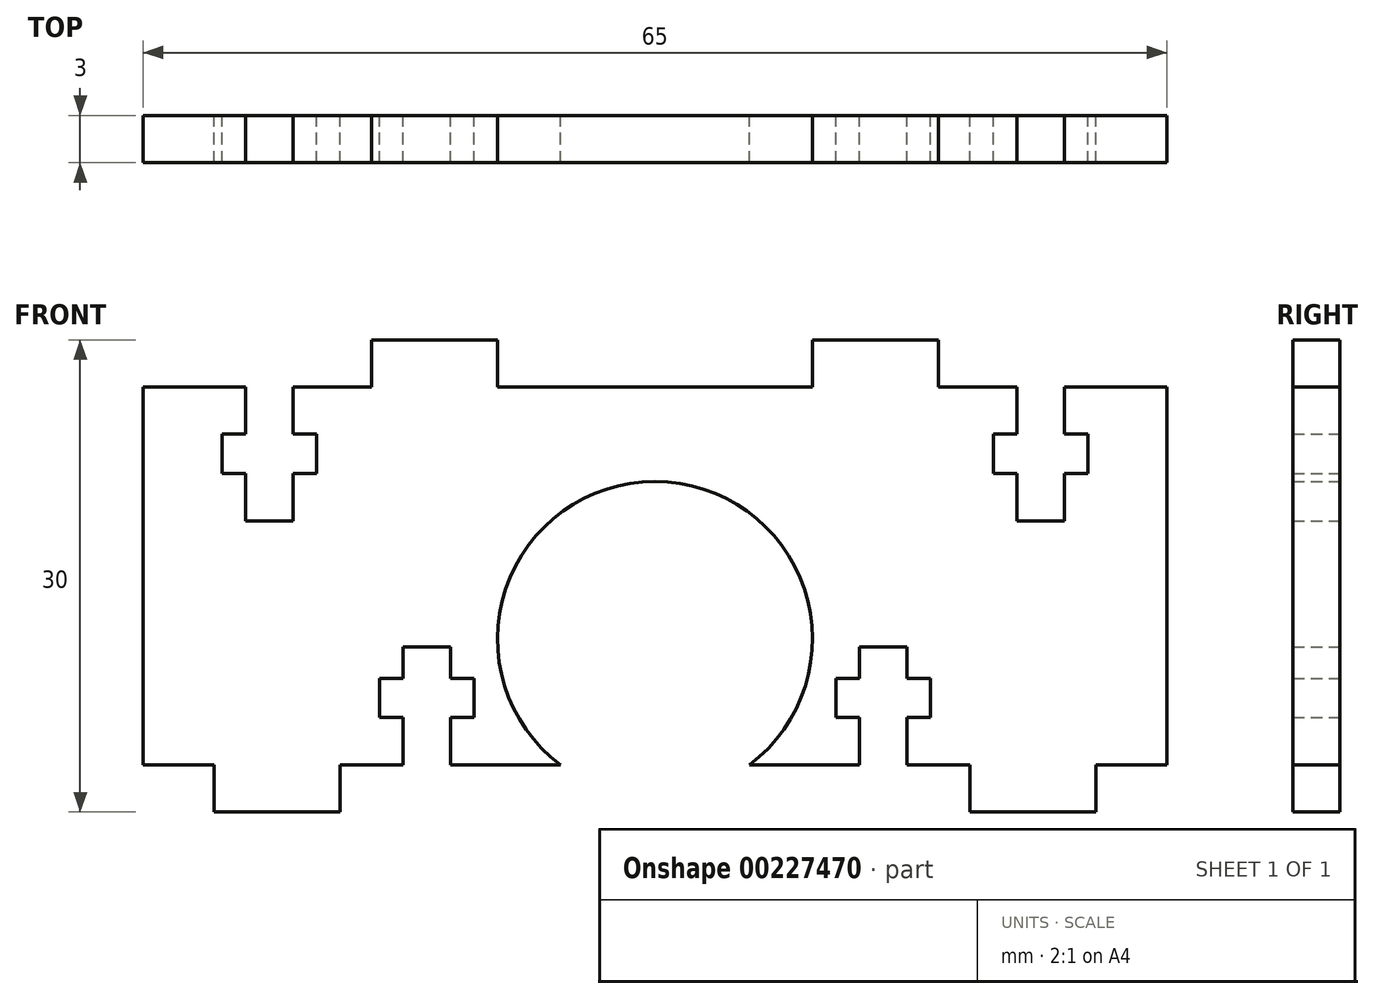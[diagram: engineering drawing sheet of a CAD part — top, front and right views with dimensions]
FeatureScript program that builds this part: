
annotation { "Feature Type Name" : "Feature", "Feature Type Description" : "" }
export const myFeature = defineFeature(function(context is Context, id is Id, definition is map)
    precondition{}
    {
        {
            var Q0;
            Q0=qCreatedBy(makeId("Front.planeOp"),FACE);
            var sketch = newSketch(context, id + "F0", { "sketchPlane" : qUnion([Q0])});
            skLineSegment(sketch, "E0.left", {"start": v(32.5, -8) * mm, "end": v(32.5, 16) * mm});
            skLineSegment(sketch, "E0.right", {"start": v(-32.5, -8) * mm, "end": v(-32.5, 16) * mm});
            skPoint(sketch, "E0.middle", {"position": v(0, 0) * mm});
            skCircle(sketch, "E1", {"center": v(0, 0) * mm, "radius": 10 * mm});
            skPoint(sketch, "E2", {"position": v(0, -8) * mm});
            skLineSegment(sketch, "E3", {"start": v(0, -8) * mm, "end": v(20, -8) * mm});
            skLineSegment(sketch, "E4", {"start": v(20, -8) * mm, "end": v(20, -11) * mm});
            skLineSegment(sketch, "E5", {"start": v(20, -11) * mm, "end": v(28, -11) * mm});
            skLineSegment(sketch, "E6", {"start": v(28, -11) * mm, "end": v(28, -8) * mm});
            skLineSegment(sketch, "E7.MirrorCS", {"start": v(0, -8) * mm, "end": v(-20, -8) * mm});
            skLineSegment(sketch, "E8.MirrorCS", {"start": v(-20, -8) * mm, "end": v(-20, -11) * mm});
            skLineSegment(sketch, "E9.MirrorCS", {"start": v(-20, -11) * mm, "end": v(-28, -11) * mm});
            skLineSegment(sketch, "E10.MirrorCS", {"start": v(-28, -11) * mm, "end": v(-28, -8) * mm});
            skLineSegment(sketch, "E11", {"start": v(32.5, -8) * mm, "end": v(28, -8) * mm});
            skLineSegment(sketch, "E12", {"start": v(-28, -8) * mm, "end": v(-32.5, -8) * mm});
            skPoint(sketch, "E13", {"position": v(0, 16) * mm});
            skLineSegment(sketch, "E14", {"start": v(-32.5, 16) * mm, "end": v(-18, 16) * mm});
            skLineSegment(sketch, "E15", {"start": v(-18, 16) * mm, "end": v(-18, 19) * mm});
            skLineSegment(sketch, "E16", {"start": v(-18, 19) * mm, "end": v(-10, 19) * mm});
            skLineSegment(sketch, "E17", {"start": v(-10, 19) * mm, "end": v(-10, 16) * mm});
            skLineSegment(sketch, "E18", {"start": v(-10, 16) * mm, "end": v(0, 16) * mm});
            skLineSegment(sketch, "E19.MirrorCS", {"start": v(10, 16) * mm, "end": v(0, 16) * mm});
            skLineSegment(sketch, "E20.MirrorCS", {"start": v(10, 19) * mm, "end": v(10, 16) * mm});
            skLineSegment(sketch, "E21.MirrorCS", {"start": v(18, 19) * mm, "end": v(10, 19) * mm});
            skLineSegment(sketch, "E22.MirrorCS", {"start": v(18, 16) * mm, "end": v(18, 19) * mm});
            skLineSegment(sketch, "E23.MirrorCS", {"start": v(32.5, 16) * mm, "end": v(18, 16) * mm});
            skSolve(sketch);
        }
        {
            var Q0;
            Q0=makeQuery(id+"F0.imprint","IMPRINT",FACE,{"disambiguationData":[TD([[makeQuery(id+"F0.imprint","IMPRINT",EDGE,{"derivedFrom":sQuery(id+"F0.wireOp",EDGE,"E0.left")}),1.0]])]});
            extrude(context, id + "F1", {"entities" : qUnion([Q0]), "depth" : 3 * mm});
        }
        {
            var Q0;
            Q0=makeQuery(id+"F1.opExtrude","CAP_FACE",FACE,{"disambiguationData":[OSD([sQuery(id+"F0.wireOp",EDGE,"E0.top"),sQuery(id+"F0.wireOp",EDGE,"E0.left"),sQuery(id+"F0.wireOp",EDGE,"E0.right"),sQuery(id+"F0.wireOp",EDGE,"E1"),sQuery(id+"F0.wireOp",EDGE,"E3"),sQuery(id+"F0.wireOp",EDGE,"E4"),sQuery(id+"F0.wireOp",EDGE,"E5"),sQuery(id+"F0.wireOp",EDGE,"E6"),sQuery(id+"F0.wireOp",EDGE,"Bye9wKvp-iTN6-aMiy-t3HV-321I6idTwAT7"),sQuery(id+"F0.wireOp",EDGE,"MaIOWbBU-8FJR-umEs-W0u1-0UBdhOL1jX3R"),sQuery(id+"F0.wireOp",EDGE,"cjjMekjN-d9GH-w392-u9fJ-7fXVraFaPUEF"),sQuery(id+"F0.wireOp",EDGE,"r4o5ajzM-Rsn6-LwNu-8ZH8-RrZPdrBqQNhf"),sQuery(id+"F0.wireOp",EDGE,"4rBLy9Cv-BTZd-DXYO-WPMD-THVSlvj0M45P"),sQuery(id+"F0.wireOp",EDGE,"0QHm3L1z-PB8E-sUM8-9Iu7-9ylB9Zyak7ZM"),sQuery(id+"F0.wireOp",EDGE,"lGSHjSAP-HDtq-xCeI-DjX7-dJADT3ItqI3i"),sQuery(id+"F0.wireOp",EDGE,"hqEljnGM-RK9Z-ywhK-KnxT-DgdnVdAw69hx"),sQuery(id+"F0.wireOp",EDGE,"3JF1scFz-tUfL-0J2I-GCU2-pg9Iem59yael"),sQuery(id+"F0.wireOp",EDGE,"VIemKg7s-0Qql-9ATH-uaDb-s28MwwDJACN2"),sQuery(id+"F0.wireOp",EDGE,"SrsuBa1K-ROI0-YVy5-osGe-RaKEGjTI8dTk"),sQuery(id+"F0.wireOp",EDGE,"fkxjX4On-I71C-g2Ab-9X9a-8QQVlJaSbmEA"),sQuery(id+"F0.wireOp",EDGE,"fKuv9ndE-aQbh-sH4q-A6gn-ncGJMZsXg4NX"),sQuery(id+"F0.wireOp",EDGE,"E7.MirrorCS"),sQuery(id+"F0.wireOp",EDGE,"E8.MirrorCS"),sQuery(id+"F0.wireOp",EDGE,"E9.MirrorCS"),sQuery(id+"F0.wireOp",EDGE,"E10.MirrorCS"),sQuery(id+"F0.wireOp",EDGE,"167239a6-6452-41fe-82d5-06518cd1e7ca0.MirrorCS"),sQuery(id+"F0.wireOp",EDGE,"4d03efd5-a7b2-448c-9269-3b157b8b6a3f0.MirrorCS"),sQuery(id+"F0.wireOp",EDGE,"4a9de9e8-4b7a-41f9-be51-9981378ba4400.MirrorCS"),sQuery(id+"F0.wireOp",EDGE,"477fae85-c943-47b6-9154-c00c6ce072b60.MirrorCS"),sQuery(id+"F0.wireOp",EDGE,"f8cb59b5-f55e-4440-885b-3b89e86697820.MirrorCS"),sQuery(id+"F0.wireOp",EDGE,"5bb5084e-da35-4d76-b03d-406c150248a20.MirrorCS"),sQuery(id+"F0.wireOp",EDGE,"8fed15e2-98f6-4966-a165-82ee8002b8fb0.MirrorCS"),sQuery(id+"F0.wireOp",EDGE,"7ee60ff3-4344-4ca1-8754-2f7ee897794d0.MirrorCS"),sQuery(id+"F0.wireOp",EDGE,"6a09c46f-801d-4278-9024-28b163129c370.MirrorCS"),sQuery(id+"F0.wireOp",EDGE,"90cf5c0c-33e3-46b7-a68c-16b02a4c827a0.MirrorCS"),sQuery(id+"F0.wireOp",EDGE,"6cdd3639-f48b-44bc-9e45-be0ea5840fc20.MirrorCS"),sQuery(id+"F0.wireOp",EDGE,"234d0976-2521-4b2c-bc8e-cd19e18f5db30.MirrorCS"),sQuery(id+"F0.wireOp",EDGE,"0711aa81-e21d-44fe-b418-f76be042628f0.MirrorCS")])],"isStart":true});
            var sketch = newSketch(context, id + "F2", { "sketchPlane" : qUnion([Q0])});
            skLineSegment(sketch, "E24", {"start": v(13, -8) * mm, "end": v(13, -5) * mm});
            skLineSegment(sketch, "E25", {"start": v(13, -5) * mm, "end": v(11.5, -5) * mm});
            skLineSegment(sketch, "E26", {"start": v(11.5, -5) * mm, "end": v(11.5, -2.5) * mm});
            skLineSegment(sketch, "E27", {"start": v(11.5, -2.5) * mm, "end": v(13, -2.5) * mm});
            skLineSegment(sketch, "E28", {"start": v(13, -2.5) * mm, "end": v(13, -0.5) * mm});
            skLineSegment(sketch, "E29", {"start": v(13, -0.5) * mm, "end": v(16, -0.5) * mm});
            skLineSegment(sketch, "E30", {"start": v(16, -0.5) * mm, "end": v(16, -2.5) * mm});
            skLineSegment(sketch, "E31", {"start": v(16, -2.5) * mm, "end": v(17.5, -2.5) * mm});
            skLineSegment(sketch, "E32", {"start": v(17.5, -2.5) * mm, "end": v(17.5, -5) * mm});
            skLineSegment(sketch, "E33", {"start": v(17.5, -5) * mm, "end": v(16, -5) * mm});
            skLineSegment(sketch, "E34", {"start": v(16, -5) * mm, "end": v(16, -8) * mm});
            skPoint(sketch, "E35", {"position": v(14.5, -8) * mm});
            skLineSegment(sketch, "E36", {"start": v(16, -8) * mm, "end": v(13, -8) * mm});
            skLineSegment(sketch, "E37.MirrorCS", {"start": v(-13, -2.5) * mm, "end": v(-13, -0.5) * mm});
            skLineSegment(sketch, "E38.MirrorCS", {"start": v(-13, -5) * mm, "end": v(-11.5, -5) * mm});
            skLineSegment(sketch, "E39.MirrorCS", {"start": v(-11.5, -5) * mm, "end": v(-11.5, -2.5) * mm});
            skLineSegment(sketch, "E40.MirrorCS", {"start": v(-16, -0.5) * mm, "end": v(-16, -2.5) * mm});
            skLineSegment(sketch, "E41.MirrorCS", {"start": v(-17.5, -5) * mm, "end": v(-16, -5) * mm});
            skLineSegment(sketch, "E42.MirrorCS", {"start": v(-11.5, -2.5) * mm, "end": v(-13, -2.5) * mm});
            skLineSegment(sketch, "E43.MirrorCS", {"start": v(-17.5, -2.5) * mm, "end": v(-17.5, -5) * mm});
            skLineSegment(sketch, "E44.MirrorCS", {"start": v(-16, -2.5) * mm, "end": v(-17.5, -2.5) * mm});
            skLineSegment(sketch, "E45.MirrorCS", {"start": v(-16, -8) * mm, "end": v(-13, -8) * mm});
            skLineSegment(sketch, "E46.MirrorCS", {"start": v(-13, -0.5) * mm, "end": v(-16, -0.5) * mm});
            skLineSegment(sketch, "E47.MirrorCS", {"start": v(-13, -8) * mm, "end": v(-13, -5) * mm});
            skPoint(sketch, "E48.MirrorP", {"position": v(-14.5, -8) * mm});
            skLineSegment(sketch, "E49.MirrorCS", {"start": v(-16, -5) * mm, "end": v(-16, -8) * mm});
            skLineSegment(sketch, "E50", {"start": v(26, 16) * mm, "end": v(26, 13) * mm});
            skLineSegment(sketch, "E51", {"start": v(26, 13) * mm, "end": v(27.5, 13) * mm});
            skLineSegment(sketch, "E52", {"start": v(27.5, 13) * mm, "end": v(27.5, 10.5) * mm});
            skLineSegment(sketch, "E53", {"start": v(27.5, 10.5) * mm, "end": v(26, 10.5) * mm});
            skLineSegment(sketch, "E54", {"start": v(26, 10.5) * mm, "end": v(26, 7.5) * mm});
            skLineSegment(sketch, "E55", {"start": v(26, 7.5) * mm, "end": v(23, 7.5) * mm});
            skLineSegment(sketch, "E56", {"start": v(23, 7.5) * mm, "end": v(23, 10.5) * mm});
            skLineSegment(sketch, "E57", {"start": v(23, 10.5) * mm, "end": v(21.5, 10.5) * mm});
            skLineSegment(sketch, "E58", {"start": v(21.5, 10.5) * mm, "end": v(21.5, 13) * mm});
            skLineSegment(sketch, "E59", {"start": v(21.5, 13) * mm, "end": v(23, 13) * mm});
            skLineSegment(sketch, "E60", {"start": v(23, 13) * mm, "end": v(23, 16) * mm});
            skLineSegment(sketch, "E61", {"start": v(23, 16) * mm, "end": v(26, 16) * mm});
            skPoint(sketch, "E62", {"position": v(24.5, 16) * mm});
            skLineSegment(sketch, "E63.MirrorCS", {"start": v(-21.5, 10.5) * mm, "end": v(-21.5, 13) * mm});
            skLineSegment(sketch, "E64.MirrorCS", {"start": v(-23, 16) * mm, "end": v(-26, 16) * mm});
            skLineSegment(sketch, "E65.MirrorCS", {"start": v(-26, 7.5) * mm, "end": v(-23, 7.5) * mm});
            skPoint(sketch, "E66.MirrorP", {"position": v(-24.5, 16) * mm});
            skLineSegment(sketch, "E67.MirrorCS", {"start": v(-21.5, 13) * mm, "end": v(-23, 13) * mm});
            skLineSegment(sketch, "E68.MirrorCS", {"start": v(-23, 7.5) * mm, "end": v(-23, 10.5) * mm});
            skLineSegment(sketch, "E69.MirrorCS", {"start": v(-23, 13) * mm, "end": v(-23, 16) * mm});
            skLineSegment(sketch, "E70.MirrorCS", {"start": v(-23, 10.5) * mm, "end": v(-21.5, 10.5) * mm});
            skLineSegment(sketch, "E71.MirrorCS", {"start": v(-26, 10.5) * mm, "end": v(-26, 7.5) * mm});
            skLineSegment(sketch, "E72.MirrorCS", {"start": v(-26, 16) * mm, "end": v(-26, 13) * mm});
            skLineSegment(sketch, "E73.MirrorCS", {"start": v(-27.5, 13) * mm, "end": v(-27.5, 10.5) * mm});
            skLineSegment(sketch, "E74.MirrorCS", {"start": v(-27.5, 10.5) * mm, "end": v(-26, 10.5) * mm});
            skLineSegment(sketch, "E75.MirrorCS", {"start": v(-26, 13) * mm, "end": v(-27.5, 13) * mm});
            skSolve(sketch);
        }
        {
            var Q0;
            Q0=makeQuery(id+"F2.imprint","IMPRINT",FACE,{"disambiguationData":[TD([[makeQuery(id+"F2.imprint","IMPRINT",EDGE,{"derivedFrom":sQuery(id+"F2.wireOp",EDGE,"E24")}),-1.0]])]});
            var Q1;
            Q1=makeQuery(id+"F2.imprint","IMPRINT",FACE,{"disambiguationData":[TD([[makeQuery(id+"F2.imprint","IMPRINT",EDGE,{"derivedFrom":sQuery(id+"F2.wireOp",EDGE,"E37.MirrorCS")}),1.0]])]});
            var Q2;
            Q2=makeQuery(id+"F2.imprint","IMPRINT",FACE,{"disambiguationData":[TD([[makeQuery(id+"F2.imprint","IMPRINT",EDGE,{"derivedFrom":sQuery(id+"F2.wireOp",EDGE,"E50")}),-1.0]])]});
            var Q3;
            Q3=makeQuery(id+"F2.imprint","IMPRINT",FACE,{"disambiguationData":[TD([[makeQuery(id+"F2.imprint","IMPRINT",EDGE,{"derivedFrom":sQuery(id+"F2.wireOp",EDGE,"E63.MirrorCS")}),1.0]])]});
            extrude(context, id + "F3", {"entities" : qUnion([Q0, Q1, Q2, Q3]), "operationType" : NewBodyOperationType.REMOVE, "endBound" : BoundingType.UP_TO_NEXT, "oppositeDirection" : true, "depth" : 25 * mm});
        }
    });
